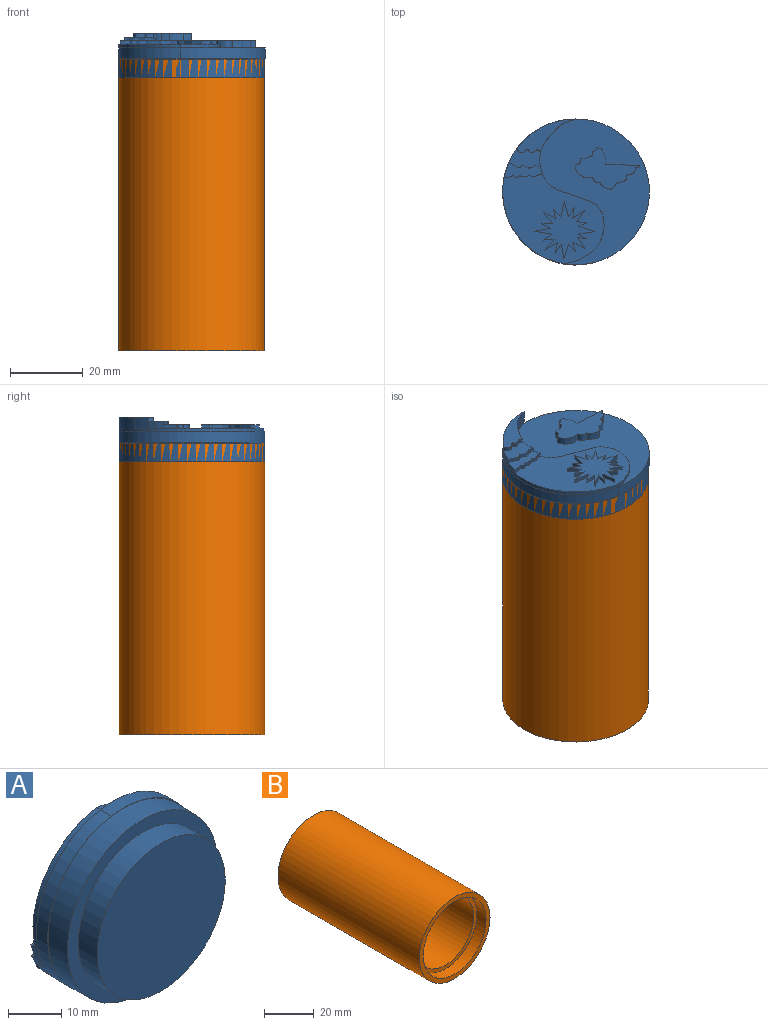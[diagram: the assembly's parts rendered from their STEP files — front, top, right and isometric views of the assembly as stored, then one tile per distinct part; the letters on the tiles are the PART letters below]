
ASSEMBLY  parts=2 mates=1
PART A: 77 faces, bbox 40.4x17.2x40 mm
  f0: plane 2.37x0.81mm, normal (0,1,0), area 0.1mm2, adj f17,f65
  f1: plane 2.72x2.2mm, normal (0,1,0), area 0.2mm2, adj f17,f64
  f2: plane 3.81x3.74mm, normal (0,1,0), area 0.2mm2, adj f18,f63
  f3: plane 1.25x0.07mm, normal (0,1,0), area 0mm2, adj f17,f59
  f4: plane 27.88x24.62mm, normal (0,1,0), area 379.5mm2, adj f17,f18,f19,f20,f21,f22,f23,f24
  f5: plane 3.59x1.11mm, normal (0,1,0), area 0.2mm2, adj f18,f53
  f6: plane 2.29x1.14mm, normal (0,1,0), area 0mm2, adj f18,f58
  f7: cylinder r=20mm len=40mm, axis (0,1,0), area 653.5mm2, adj f8,f11,f16
  f8: plane 40x40mm, normal (0,-1,0), area 338.8mm2, adj f7,f9
  f9: cylinder r=17.09mm len=34.19mm, axis (0,1,0), area 537mm2, adj f8,f10
  f10: plane 34.19x34.19mm, normal (0,-1,0), area 917.9mm2, adj f9
  f11: plane 40.05x23.38mm, normal (0,-1,0), area 13mm2, adj f7,f14
  f12: plane 39.76x20.06mm, normal (0,1,0), area 2.2mm2, adj f15,f18
  f13: plane 40.05x30.27mm, normal (0,1,0), area 600.9mm2, adj f14,f17,f68,f69,f70,f71,f72,f73
  f14: cylinder r=20.02mm len=40.05mm, axis (0,-1,0), area 199.7mm2, adj f11,f13,f15
  f15: cylinder r=20mm len=39.76mm, axis (0,-1,0), area 179.6mm2, adj f12,f14,f16
  f16: plane 39.76x20.06mm, normal (0,-1,0), area 2.2mm2, adj f7,f15
  f17: extruded ~39.76x17.67mm, area 91.3mm2, adj f0,f1,f3,f4,f13,f18,f52,f56
  f18: cylinder r=20mm len=39.76mm, axis (0,1,0), area 77.2mm2, adj f2,f4,f5,f6,f12,f17,f58,f60
  f19: plane 2.7x1mm, normal (0.09,0,-1), area 2.7mm2, adj f4,f20,f50,f51
  f20: plane 3.07x2.32mm, normal (0.8,0,0.6), area 3.8mm2, adj f4,f19,f21,f51
  f21: plane 3.36x2.12mm, normal (-0.53,0,-0.85), area 4mm2, adj f4,f20,f22,f51
  f22: plane 2.96x1mm, normal (0.99,0,0.14), area 3mm2, adj f4,f21,f23,f51
  f23: plane 2.46x1.61mm, normal (-0.84,0,-0.55), area 2.9mm2, adj f4,f22,f24,f51
  f24: plane 4.13x1.12mm, normal (0.97,0,-0.26), area 4.3mm2, adj f4,f23,f25,f51
  f25: plane 4.21x1mm, normal (-0.97,0,-0.22), area 4.3mm2, adj f4,f24,f26,f51
  f26: plane 1.98x1.93mm, normal (0.72,0,-0.7), area 2.8mm2, adj f4,f25,f27,f51
  f27: plane 2.52x1mm, normal (-0.99,0,0.16), area 2.6mm2, adj f4,f26,f28,f51
  f28: plane 3.32x1.85mm, normal (0.49,0,-0.87), area 3.8mm2, adj f4,f27,f29,f51
  f29: plane 3.18x2.55mm, normal (-0.78,0,0.63), area 4.1mm2, adj f4,f28,f30,f51
  f30: plane 2.93x1mm, normal (0,0,-1), area 2.9mm2, adj f4,f29,f31,f51
  f31: plane 2.48x1.37mm, normal (-0.48,0,0.88), area 2.8mm2, adj f4,f30,f32,f51
  f32: plane 4.59x1mm, normal (-0.16,0,-0.99), area 4.6mm2, adj f4,f31,f33,f51
  f33: plane 4.69x1mm, normal (-0.16,0,0.99), area 4.7mm2, adj f4,f32,f34,f51
  f34: plane 2.21x1.64mm, normal (-0.6,0,-0.8), area 2.8mm2, adj f4,f33,f35,f51
  f35: plane 2.96x1mm, normal (0.06,0,1), area 3mm2, adj f4,f34,f36,f51
  f36: plane 3.03x2.67mm, normal (-0.75,0,-0.66), area 4mm2, adj f4,f35,f37,f51
  f37: plane 3.6x2.2mm, normal (0.52,0,0.85), area 4.2mm2, adj f4,f36,f38,f51
  f38: plane 2.91x1mm, normal (-0.98,0,-0.2), area 3mm2, adj f4,f37,f39,f51
  f39: plane 2.44x1.66mm, normal (0.83,0,0.56), area 2.9mm2, adj f4,f38,f40,f51
  f40: plane 4.09x1mm, normal (-0.99,0,0.16), area 4.1mm2, adj f4,f39,f41,f51
  f41: plane 4.05x1.25mm, normal (0.96,0,0.3), area 4.2mm2, adj f4,f40,f42,f51
  f42: plane 1.99x1.95mm, normal (-0.71,0,0.7), area 2.8mm2, adj f4,f41,f43,f51
  f43: plane 2.49x1mm, normal (0.96,0,-0.29), area 2.6mm2, adj f4,f42,f44,f51
  f44: plane 3.27x1.61mm, normal (-0.44,0,0.9), area 3.6mm2, adj f4,f43,f45,f51
  f45: plane 3.04x1.93mm, normal (0.84,0,-0.54), area 3.6mm2, adj f4,f44,f46,f51
  f46: plane 2.56x1mm, normal (-0.19,0,0.98), area 2.6mm2, adj f4,f45,f47,f51
  f47: plane 2.22x1.32mm, normal (0.51,0,-0.86), area 2.6mm2, adj f4,f46,f48,f51
  f48: plane 4.28x1mm, normal (0.16,0,0.99), area 4.3mm2, adj f4,f47,f49,f51
  f49: plane 4.28x1.39mm, normal (0.31,0,-0.95), area 4.5mm2, adj f4,f48,f50,f51
  f50: plane 2.05x1.07mm, normal (0.46,0,0.89), area 2.3mm2, adj f4,f19,f49,f51
  f51: plane 16.54x15.83mm, normal (0,1,0), area 89.7mm2, adj f19,f20,f21,f22,f23,f24,f25,f26
  f52: plane 2x1mm, normal (0.96,0,-0.28), area 2.1mm2, adj f17,f54,f55,f56
  f53: extruded ~3.59x1.11mm, area 3.8mm2, adj f5,f54,f55,f58
  f54: extruded ~10.53x1mm, area 11.4mm2, adj f4,f52,f53,f55
  f55: plane 10.53x3.96mm, normal (0,1,0), area 27.3mm2, adj f52,f53,f54,f57
  f56: plane 2.02x0.59mm, normal (0,-1,0), area 0.1mm2, adj f17,f52
  f57: extruded ~8.85x1.25mm, area 9.8mm2, adj f17,f55,f58,f61
  f58: extruded ~2.28x2mm, area 5.1mm2, adj f6,f18,f53,f57,f61
  f59: extruded ~2x1.24mm, area 2.5mm2, adj f3,f17,f61
  f60: extruded ~2x1.92mm, area 4.6mm2, adj f18,f61,f63
  f61: plane 8.94x5.55mm, normal (0,1,0), area 32.7mm2, adj f17,f18,f57,f58,f59,f60,f62
  f62: extruded ~6.47x1.34mm, area 8.2mm2, adj f17,f61,f63,f67
  f63: extruded ~3.77x3.71mm, area 15.9mm2, adj f2,f18,f60,f62,f67
  f64: extruded ~3x2.66mm, area 10.3mm2, adj f1,f17,f67
  f65: extruded ~3x2.33mm, area 7.4mm2, adj f0,f17,f66,f67
  f66: extruded ~7.31x3mm, area 22.4mm2, adj f18,f65,f67
  f67: plane 15.99x9.39mm, normal (0,1,0), area 46.7mm2, adj f17,f18,f62,f63,f64,f65,f66
  f68: plane 9.33x2mm, normal (0.03,0,-1), area 18.7mm2, adj f13,f69,f75,f76
  f69: extruded ~4.49x2mm, area 9.8mm2, adj f13,f68,f70,f76
  f70: extruded ~5.41x2.84mm, area 14mm2, adj f13,f69,f71,f76
  f71: extruded ~2x1.97mm, area 5.4mm2, adj f13,f70,f72,f76
  f72: extruded ~4.78x3.37mm, area 13.5mm2, adj f13,f71,f73,f76
  f73: extruded ~2.13x2mm, area 6.7mm2, adj f13,f72,f74,f76
  f74: extruded ~4.27x2mm, area 11.3mm2, adj f13,f73,f75,f76
  f75: extruded ~6.49x4.94mm, area 18.3mm2, adj f13,f68,f74,f76
  f76: plane 17.65x11.38mm, normal (0,1,0), area 92.2mm2, adj f68,f69,f70,f71,f72,f73,f74,f75
PART B: 7 faces, bbox 40x80x40 mm
  f0: cylinder r=20mm len=80mm, axis (0,1,0), area 10053.1mm2, adj f1,f2
  f1: plane 40x40mm, normal (0,-1,0), area 261.4mm2, adj f0,f3
  f2: plane 40x40mm, normal (0,1,0), area 1256.6mm2, adj f0
  f3: cylinder r=17.8mm len=35.6mm, axis (0,-1,0), area 581.5mm2, adj f1,f4
  f4: plane 35.6x35.6mm, normal (0,-1,0), area 191mm2, adj f3,f6
  f5: plane 32x32mm, normal (0,-1,0), area 804.2mm2, adj f6
  f6: cylinder r=16mm len=70.8mm, axis (0,1,0), area 7117.6mm2, adj f4,f5
PLACE A rot(axis=(1,0,0),90deg) t=(-16.33,-44.03,56.26)mm
PLACE B rot(axis=(-1,0,0),90deg) t=(-16.33,-44.03,-23.87)mm
MATE slider A.f7 <-> B.f0  axis (0,0,1) through (-16.33,-44.03,48.56)mm
